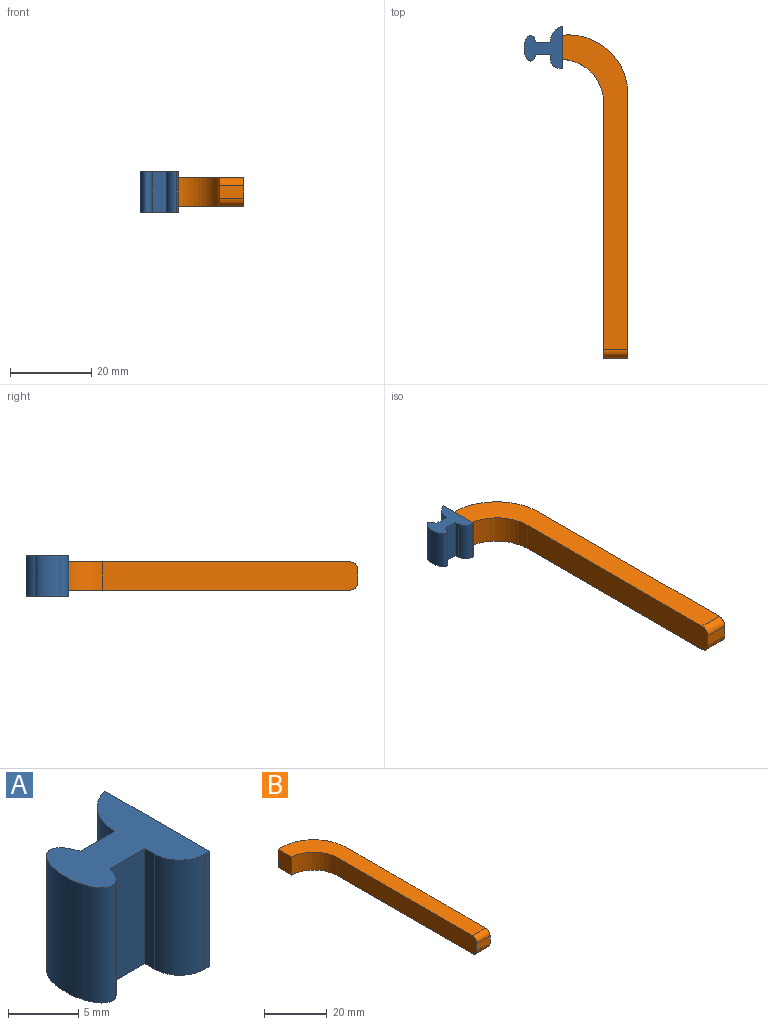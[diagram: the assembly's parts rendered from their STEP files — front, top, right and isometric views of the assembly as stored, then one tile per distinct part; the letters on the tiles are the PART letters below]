
ASSEMBLY  parts=2 mates=1
PART A: 11 faces, bbox 9.4x10.5x10 mm
  f0: plane 10x3.48mm, normal (0,-1,0), area 34.8mm2, adj f1,f6,f7,f8
  f1: plane 10x1mm, normal (-1,0,0), area 10mm2, adj f0,f6,f7,f10
  f2: plane 10x0.5mm, normal (0,-1,0), area 5mm2, adj f3,f6,f7,f10
  f3: plane 10.5x10mm, normal (1,0,0), area 105mm2, adj f2,f6,f7,f9
  f4: plane 10x0.13mm, normal (-1,0,0), area 1.3mm2, adj f5,f6,f7,f9
  f5: plane 10x3.48mm, normal (0,1,0), area 34.8mm2, adj f4,f6,f7,f8
  f6: plane 10.5x9.44mm, normal (0,0,1), area 52.6mm2, adj f0,f1,f2,f3,f4,f5,f8,f9
  f7: plane 10.5x9.44mm, normal (0,0,-1), area 52.6mm2, adj f0,f1,f2,f3,f4,f5,f8,f9
  f8: extruded ~10x6.21mm, area 121.1mm2, adj f0,f5,f6,f7
  f9: cylinder r=4mm len=10mm, axis (0,0,1), area 52.7mm2, adj f3,f4,f6,f7
  f10: cylinder r=2.5mm len=10mm, axis (0,0,-1), area 39.3mm2, adj f1,f2,f6,f7
PART B: 10 faces, bbox 16.1x79.7x7 mm
  f0: cylinder r=14.67mm len=16.15mm, axis (0,0,-1), area 171.7mm2, adj f1,f5,f6,f7
  f1: plane 7x6mm, normal (-1,0,0), area 42mm2, adj f0,f2,f6,f7
  f2: cylinder r=10.6mm len=10.59mm, axis (0,0,-1), area 113.4mm2, adj f1,f3,f6,f7
  f3: plane 63x7mm, normal (-1,0,0), area 439.3mm2, adj f2,f4,f6,f7,f8,f9
  f4: plane 6x3mm, normal (0,-1,0), area 18mm2, adj f3,f5,f8,f9
  f5: plane 65x7mm, normal (1,0,0), area 453.3mm2, adj f0,f4,f6,f7,f8,f9
  f6: plane 77.67x16.15mm, normal (0,0,1), area 505.5mm2, adj f0,f1,f2,f3,f5,f9
  f7: plane 77.67x16.15mm, normal (0,0,-1), area 505.5mm2, adj f0,f1,f2,f3,f5,f8
  f8: cylinder r=2mm len=6mm, axis (1,0,0), area 18.8mm2, adj f3,f4,f5,f7
  f9: cylinder r=2mm len=6mm, axis (-1,0,0), area 18.8mm2, adj f3,f4,f5,f6
PLACE A t=(-8.25,49.24,10.39)mm
PLACE B t=(4.89,-21.55,11.89)mm
MATE parallel A.f3 <-> B.f1  axis (1,0,0) through (-8.25,49.24,15.39)mm
